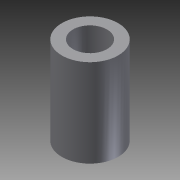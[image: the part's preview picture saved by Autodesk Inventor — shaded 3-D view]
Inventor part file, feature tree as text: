
AUTODESK INVENTOR PART (.ipt)
format: ipt  version: 2014 SP1 (Build 180222100, 222)  size: 92,160 bytes
history: native  units: in
note: dims shown in document units (in); Inventor stores cm internally (conversion verified against a paired STEP export)
features: other x1, imported_body x1, extrude x1, sketch x1
ambient origin geometry x8: Origin, YZ Plane, XZ Plane, XY Plane, X Axis, Y Axis, Z Axis, Center Point
bodies: Body1 (feature_tree)
feature tree (4):
  parser-record x1  (decoder bookkeeping rows leaked as tree rows — omitted from the tree; the rows remain in map.json)
  imported_body  "Base1"
  extrude  "Extrusion1"  Depth=1.0in TaperAngle=0.0deg
  sketch  "Sketch1"  dims[d0=0.32in d1=1.0in d2=0.0in]
